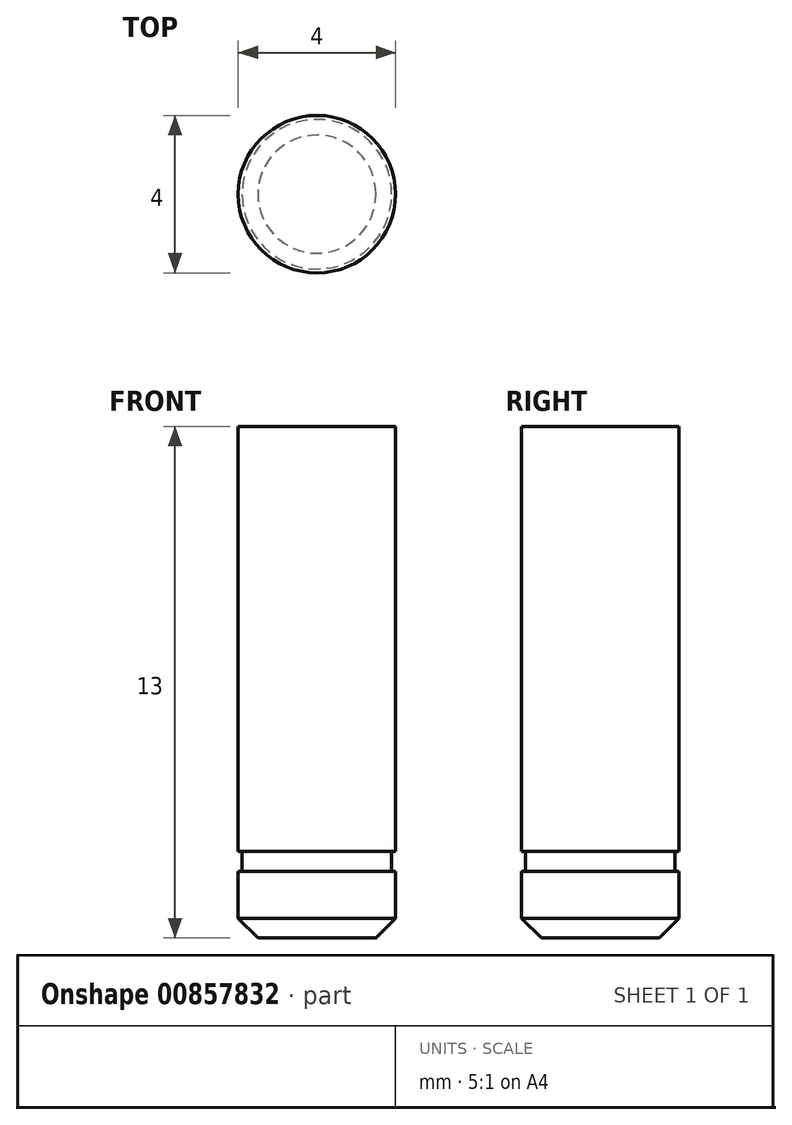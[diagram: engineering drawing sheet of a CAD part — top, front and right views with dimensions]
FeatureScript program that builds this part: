
annotation { "Feature Type Name" : "Feature", "Feature Type Description" : "" }
export const myFeature = defineFeature(function(context is Context, id is Id, definition is map)
    precondition{}
    {
        {
            var Q0;
            Q0=qCreatedBy(makeId("Front.planeOp"),FACE);
            var sketch = newSketch(context, id + "F0", { "sketchPlane" : qUnion([Q0])});
            skLineSegment(sketch, "E0", {"start": v(0, 0) * mm, "end": v(-2, 0) * mm});
            skLineSegment(sketch, "E1", {"start": v(-2, 0) * mm, "end": v(-2, 1.7) * mm});
            skLineSegment(sketch, "E2", {"start": v(-2, 13) * mm, "end": v(0, 13) * mm});
            skLineSegment(sketch, "E3", {"start": v(0, 13) * mm, "end": v(0, 0) * mm});
            skLineSegment(sketch, "E4", {"start": v(-2, 2.2) * mm, "end": v(-1.9, 2.2) * mm});
            skLineSegment(sketch, "E5", {"start": v(-1.9, 2.2) * mm, "end": v(-1.9, 1.7) * mm});
            skLineSegment(sketch, "E6", {"start": v(-1.9, 1.7) * mm, "end": v(-2, 1.7) * mm});
            skLineSegment(sketch, "E7.trimOffspring", {"start": v(-2, 2.2) * mm, "end": v(-2, 13) * mm});
            skSolve(sketch);
        }
        {
            var Q0;
            Q0=makeQuery(id+"F0.imprint","IMPRINT",FACE,{"disambiguationData":[TD([[makeQuery(id+"F0.imprint","IMPRINT",EDGE,{"derivedFrom":sQuery(id+"F0.wireOp",EDGE,"E0")}),-1.0]])]});
            var Q1;
            Q1=sQuery(id+"F0.wireOp",EDGE,"E3");
            revolve(context, id + "F1", {"surfaceOperationType" : NewSurfaceOperationType.NEW, "entities" : qUnion([Q0]), "axis" : qUnion([Q1]), "revolveType" : RevolveType.FULL});
        }
        {
            var Q0;
            Q0=makeQuery(id+"F1.opRevolve","SWEPT_EDGE",EDGE,{"disambiguationData":[OSD([sQuery(id+"F0.wireOp",EDGE,"E0"),sQuery(id+"F0.wireOp",EDGE,"E1")])]});
            chamfer(context, id + "F2", {"entities" : qUnion([Q0]), "width" : 0.5 * mm, "tangentPropagation" : true});
        }
    });
